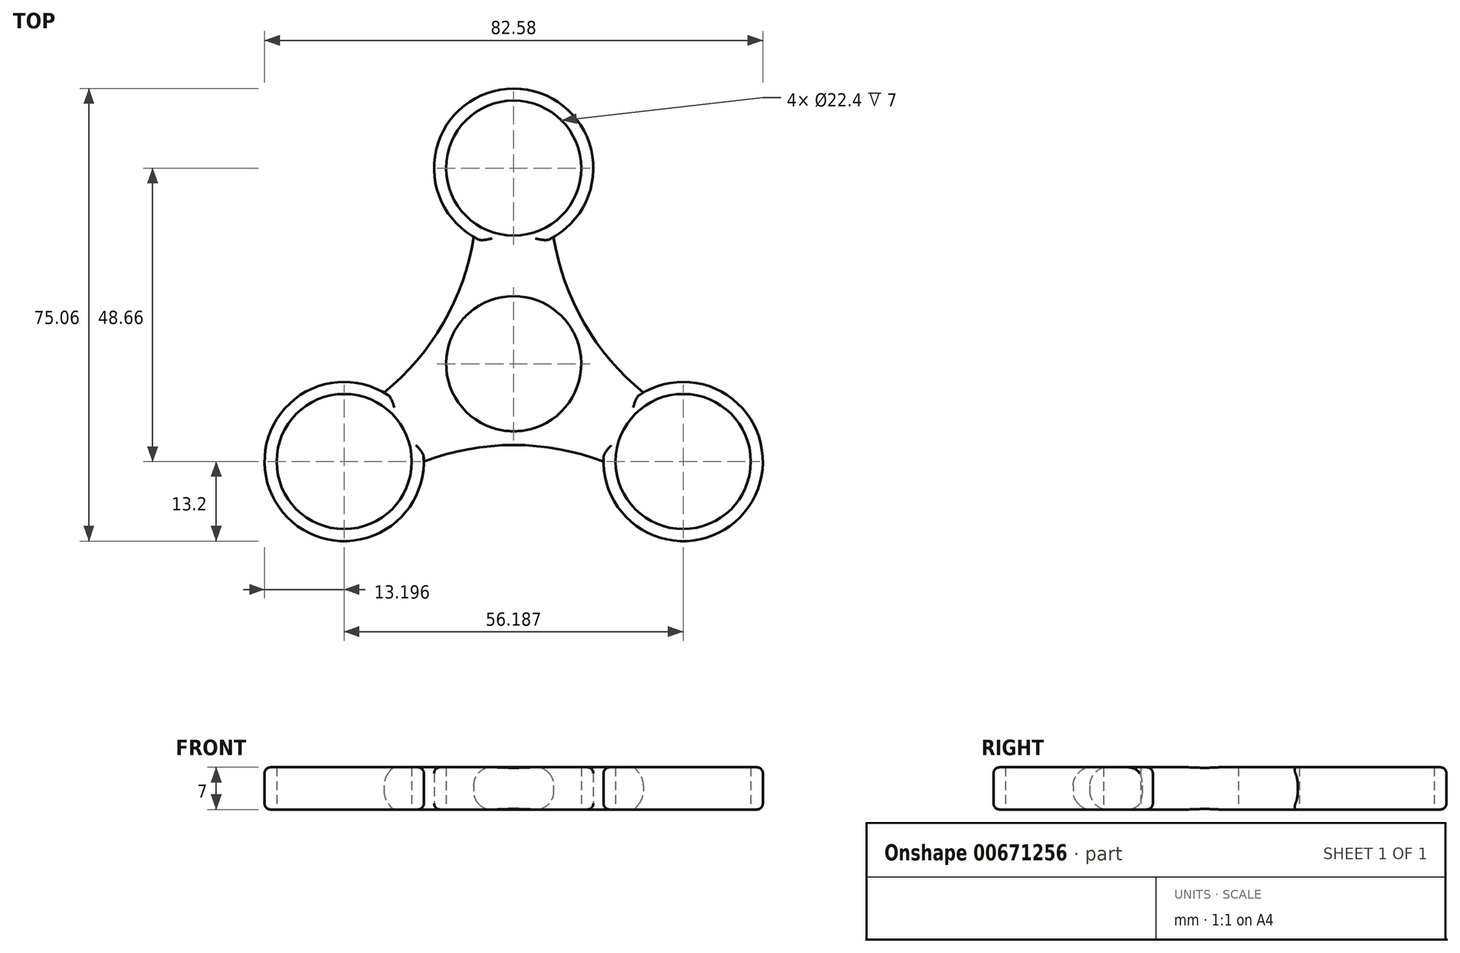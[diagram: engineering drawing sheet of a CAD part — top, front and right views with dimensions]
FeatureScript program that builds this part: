
annotation { "Feature Type Name" : "Feature", "Feature Type Description" : "" }
export const myFeature = defineFeature(function(context is Context, id is Id, definition is map)
    precondition{}
    {
        {
            var Q0;
            Q0=qCreatedBy(makeId("Top.planeOp"),FACE);
            var sketch = newSketch(context, id + "F0", { "sketchPlane" : qUnion([Q0])});
            skCircle(sketch, "E0", {"center": v(0, 0) * mm, "radius": 11.2 * mm});
            skCircle(sketch, "E1", {"center": v(0, 32.44) * mm, "radius": 11.2 * mm});
            skArc(sketch, "E2", {"start": v(6.6, 21) * mm, "mid": v(0, 45.64) * mm, "end": v(-6.6, 21) * mm});
            skCircle(sketch, "E3.1.0", {"center": v(-28.1, -16.22) * mm, "radius": 11.2 * mm});
            skArc(sketch, "E3.1.1", {"start": v(-21.5, -4.79) * mm, "mid": v(-39.53, -22.82) * mm, "end": v(-14.9, -16.22) * mm});
            skCircle(sketch, "E3.2.0", {"center": v(28.1, -16.22) * mm, "radius": 11.2 * mm});
            skArc(sketch, "E3.2.1", {"start": v(14.9, -16.22) * mm, "mid": v(39.53, -22.82) * mm, "end": v(21.5, -4.79) * mm});
            skLineSegment(sketch, "E4", {"start": v(5.6, 22.74) * mm, "end": v(6.6, 21) * mm, "construction": true});
            skLineSegment(sketch, "E5", {"start": v(-18.4, -10.62) * mm, "end": v(-16.66, -9.62) * mm, "construction": true});
            skLineSegment(sketch, "E6", {"start": v(9.7, 5.6) * mm, "end": v(11.68, 6.74) * mm, "construction": true});
            skArc(sketch, "E7", {"start": v(6.6, 21) * mm, "mid": v(11.68, 6.74) * mm, "end": v(21.5, -4.79) * mm});
            skArc(sketch, "E8.1.0", {"start": v(-21.5, -4.79) * mm, "mid": v(-11.68, 6.74) * mm, "end": v(-6.6, 21) * mm});
            skArc(sketch, "E8.2.0", {"start": v(14.9, -16.22) * mm, "mid": v(0, -13.48) * mm, "end": v(-14.9, -16.22) * mm});
            skLineSegment(sketch, "E9.trimOffspring", {"start": v(21.5, -4.79) * mm, "end": v(22.5, -6.52) * mm, "construction": true});
            skSolve(sketch);
        }
        {
            var Q0;
            Q0 = qSketchRegion(id + "F0", true);
            extrude(context, id + "F1", {"entities" : qUnion([Q0]), "depth" : 7 * mm, "offsetDistance" : 25 * mm});
        }
        {
            var Q0;
            Q0=makeQuery(id+"F1.opExtrude","CAP_EDGE",EDGE,{"disambiguationData":[OSD([sQuery(id+"F0.wireOp",EDGE,"E3.1.1")])],"isStart":false});
            var Q1;
            Q1=makeQuery(id+"F1.opExtrude","CAP_EDGE",EDGE,{"disambiguationData":[OSD([sQuery(id+"F0.wireOp",EDGE,"E3.2.1")])],"isStart":false});
            var Q2;
            Q2=makeQuery(id+"F1.opExtrude","CAP_EDGE",EDGE,{"disambiguationData":[OSD([sQuery(id+"F0.wireOp",EDGE,"E2")])],"isStart":false});
            var Q3;
            Q3=makeQuery(id+"F1.opExtrude","CAP_EDGE",EDGE,{"disambiguationData":[OSD([sQuery(id+"F0.wireOp",EDGE,"E2")])],"isStart":true});
            var Q4;
            Q4=makeQuery(id+"F1.opExtrude","CAP_EDGE",EDGE,{"disambiguationData":[OSD([sQuery(id+"F0.wireOp",EDGE,"E3.2.1")])],"isStart":true});
            var Q5;
            Q5=makeQuery(id+"F1.opExtrude","CAP_EDGE",EDGE,{"disambiguationData":[OSD([sQuery(id+"F0.wireOp",EDGE,"E3.1.1")])],"isStart":true});
            fillet(context, id + "F2", {"entities" : qUnion([Q0, Q1, Q2, Q3, Q4, Q5]), "radius" : 1 * mm, "tangentPropagation" : true, "allowEdgeOverflow" : false});
        }
        {
            var Q0;
            Q0=makeQuery(id+"F1.opExtrude","CAP_EDGE",EDGE,{"disambiguationData":[OSD([sQuery(id+"F0.wireOp",EDGE,"E8.2.0")])],"isStart":false});
            var Q1;
            Q1=makeQuery(id+"F1.opExtrude","CAP_EDGE",EDGE,{"disambiguationData":[OSD([sQuery(id+"F0.wireOp",EDGE,"E8.2.0")])],"isStart":true});
            var Q2;
            Q2=makeQuery(id+"F1.opExtrude","CAP_EDGE",EDGE,{"disambiguationData":[OSD([sQuery(id+"F0.wireOp",EDGE,"E7")])],"isStart":false});
            var Q3;
            Q3=makeQuery(id+"F1.opExtrude","CAP_EDGE",EDGE,{"disambiguationData":[OSD([sQuery(id+"F0.wireOp",EDGE,"E8.1.0")])],"isStart":false});
            var Q4;
            Q4=makeQuery(id+"F1.opExtrude","CAP_EDGE",EDGE,{"disambiguationData":[OSD([sQuery(id+"F0.wireOp",EDGE,"E8.1.0")])],"isStart":true});
            var Q5;
            Q5=makeQuery(id+"F1.opExtrude","CAP_EDGE",EDGE,{"disambiguationData":[OSD([sQuery(id+"F0.wireOp",EDGE,"E7")])],"isStart":true});
            fillet(context, id + "F3", {"entities" : qUnion([Q0, Q1, Q2, Q3, Q4, Q5]), "radius" : 3 * mm, "tangentPropagation" : true, "allowEdgeOverflow" : false});
        }
    });
